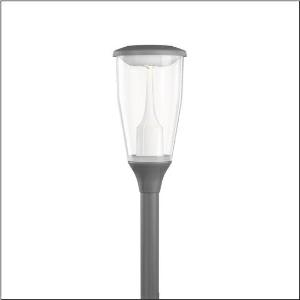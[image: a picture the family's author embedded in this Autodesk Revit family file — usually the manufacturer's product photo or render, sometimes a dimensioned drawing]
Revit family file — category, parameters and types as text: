
# Revit family: dl_11_iq___st1_2a_5xa5575mf14hp00022_5a95
name_source: partatom
category: Lighting Fixtures
units: mm (PartAtom-declared; Revit-internal decimal feet)

## family parameters
Cut with Voids When Loaded = No
Host = Face
Light Source = No
Part Type = Normal
Room Calculation Point = No
Round Connector Dimension = Use Diameter
Shared = No

## types (1)
- --- (1 x LED, 4340 lm, 33.6 W, 2700K)
    Apparent Load = 34 VA
    CIE Flux Codes = 33 63 91 94 100
    Color Rendering = 70
    Color Temperature = 2700K
    Default Elevation = 1800 mm
    Description = DL 11 iQ, mast luminaire, Module 540 iQ-SR, primary light control with 3 zone facetted reflector, of plastic, silver coated, highly specular, structured, primary optical cover: cover, of PMMA, transparent, light distribution: ST1.2a, light emission: direct distribution, primary light characteristic: asymmetric, installation type: post-top, LED, High Power LED, light colour: 727, colour temperature: 2700K, control: Street-Remote, Auto-Match, Temp-Guard, Lumen-Switch, Night-Set, Smart-Wire, Light-Fading, Desk-Remote (wireless, voltage-free reading and setting of iQ features in the workshop via application-optimized NFC function/RFID function), optimised constant luminous flux control (CLO 2.0), mains connection: 220..240V, AC, 50/60Hz, connection cable pre-assembled, cable length: 5,5m, wiring characteristics: H07RN-F, 5-core, 1.5mm², start of lifetime: 34W, end of service life: 36W, luminaire housing, upper part, of diecast aluminium, coated, Siteco® metallic grey (DB 702S), spigot size: 76mm (post-top), post-top mast mounting element, of diecast aluminium, coated, Siteco® metallic grey (DB 702S), Module 540 iQ-SR, traffic white (RAL 9016), equipment: Power, protection rating (complete): IP66, insulation class (complete): insulation class II (safety insulation), certification: CE, ENEC, ENEC+, VDE, packaging unit: 1 piece

Light Distribution: ST1.2a
    Height = 665 mm
    Lamp = 1 x LED
    Lamp Light Flux = 4340 lm
    Lamp Power = 33.6 W
    Lamp count = 1
    Length = 334 mm
    Luminous efficacy = 129 lm/W
    Manufacturer = Siteco
    ModVariant = No
    Model = 5XA5575MF14HP00022
    Number of Poles = 1
    OnlyDefault = Yes
    Power Factor = 1
    Product Name = DL 11 iQ | ST1.2a
    Product group = mast luminaire | pylon top
    ProductGroupID = 6100
    Protection Class = Protection class II
    Protection Degree = IP 66
    RLX_Detail_Level = 1
    RLX_Emergency_Light_Flux = 0 lm
    RLX_Emergency_Type = 0
    RLX_Emergency_Type_DB = No
    RlxData = <blob elided: 155325 chars, md5=8a998637>
    Socket = socket
    Standby Power = 0 W
    System Light Flux = 4340 lm
    System Power = 34 W
    Type Comments = factory setting: luminous flux: 100 % | dim-lin: 254 | 695 mA
    Type Image = l_1258354.jpg
    URL = http://relux.com
    VarID = @adj_019845
    Voltage = 0 V
    Weight = 0.00 kg
    Width = 0 mm  [stored 0 ft]

note: [stored X ft] marks values corroborated as IEEE doubles in the binary element streams (Revit-internal decimal feet)

## geometry (parser evidence)
native form markers: Blend x4, Sweep x10
no freeform markers — native parametric forms only
